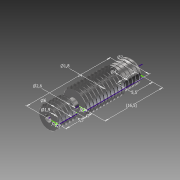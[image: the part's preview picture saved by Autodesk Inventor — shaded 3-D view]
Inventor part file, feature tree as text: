
AUTODESK INVENTOR PART (.ipt)
format: ipt  version: 2015 (Build 190159000, 159)  size: 620,544 bytes
history: native  units: mm
features: other x3, sketch x2, thread x2, revolve x1, extrude x1, chamfer x1
ambient origin geometry x8: Origin, YZ Plane, XZ Plane, XY Plane, X Axis, Y Axis, Z Axis, Center Point
bodies: Body1 (feature_tree)
feature tree (10):
  other  "Твердое тело1"
  sketch  "Эскиз1"
  revolve  "Вращение1"
  thread  "Резьба1"
  other  "Пружина1"
  thread  "Резьба2"
  other  "Пружина2"
  extrude  "Выдавливание1"  Depth=2.0mm
  chamfer  "Фаска1"  Distance=7.0mm
  sketch  "Эскиз2"
